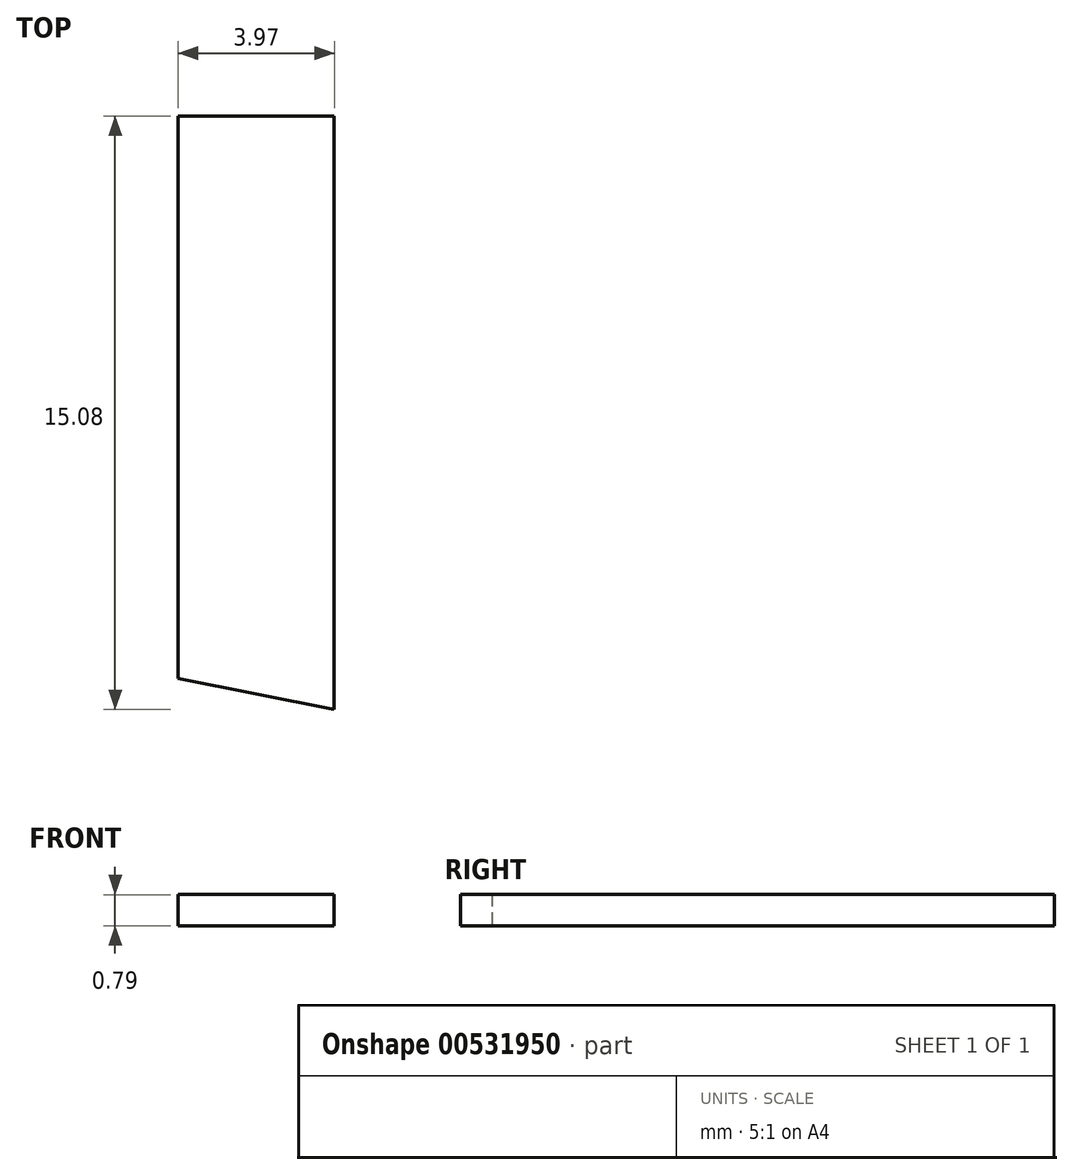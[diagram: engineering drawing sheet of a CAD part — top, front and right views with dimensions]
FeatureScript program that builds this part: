
annotation { "Feature Type Name" : "Feature", "Feature Type Description" : "" }
export const myFeature = defineFeature(function(context is Context, id is Id, definition is map)
    precondition{}
    {
        {
            var Q0;
            Q0=qCreatedBy(makeId("Top.planeOp"),FACE);
            var sketch = newSketch(context, id + "F0", { "sketchPlane" : qUnion([Q0])});
            skLineSegment(sketch, "E0", {"start": v(-19.05, 38.92) * mm, "end": v(-15.08, 38.92) * mm});
            skLineSegment(sketch, "E1", {"start": v(-15.08, 38.92) * mm, "end": v(-15.08, 23.84) * mm});
            skLineSegment(sketch, "E2", {"start": v(-19.05, 38.92) * mm, "end": v(-19.05, 24.64) * mm});
            skLineSegment(sketch, "E3", {"start": v(-19.05, 24.64) * mm, "end": v(-15.08, 23.84) * mm});
            skSolve(sketch);
        }
        {
            var Q0;
            Q0 = qSketchRegion(id + "F0", true);
            extrude(context, id + "F1", {"entities" : qUnion([Q0]), "depth" : 0.8 * mm, "offsetDistance" : 25.4 * mm});
        }
    });
